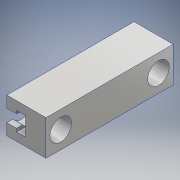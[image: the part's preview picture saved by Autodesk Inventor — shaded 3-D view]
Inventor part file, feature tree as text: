
AUTODESK INVENTOR PART (.ipt)
format: ipt  version: 2016 (Build 200138000, 138)  size: 140,288 bytes
history: native  units: mm
features: extrude x4, sketch x3
ambient origin geometry x8: Origin, YZ Plane, XZ Plane, XY Plane, X Axis, Y Axis, Z Axis, Center Point
bodies: Solid1 (feature_tree)
feature tree (7):
  extrude  "Extrusion1"  Depth=20.0mm
  sketch  "Sketch2"  dims[d2=65.0mm d3=0.0mm d4=6.5mm]
  extrude  "Extrusion2"  Depth=65.0mm
  extrude  "Extrusion3"  Depth=10.0mm
  extrude  "Extrusion4"  Depth=10.0mm
  sketch  "Sketch1"  dims[d0=18.0mm d1=20.0mm]
  sketch  "Sketch4"  dims[d5=6.5mm d8=11.0mm d9=11.0mm d10=50.0mm d11=0.0mm d12=26.0mm d13=0.0mm d26=25.0mm d27=25.0mm d28=6.4mm d29=4.5mm d30=9.6mm d31=5.0mm d32=10.0mm d33=0.0mm d15=1.0mm d16=1.0mm]
